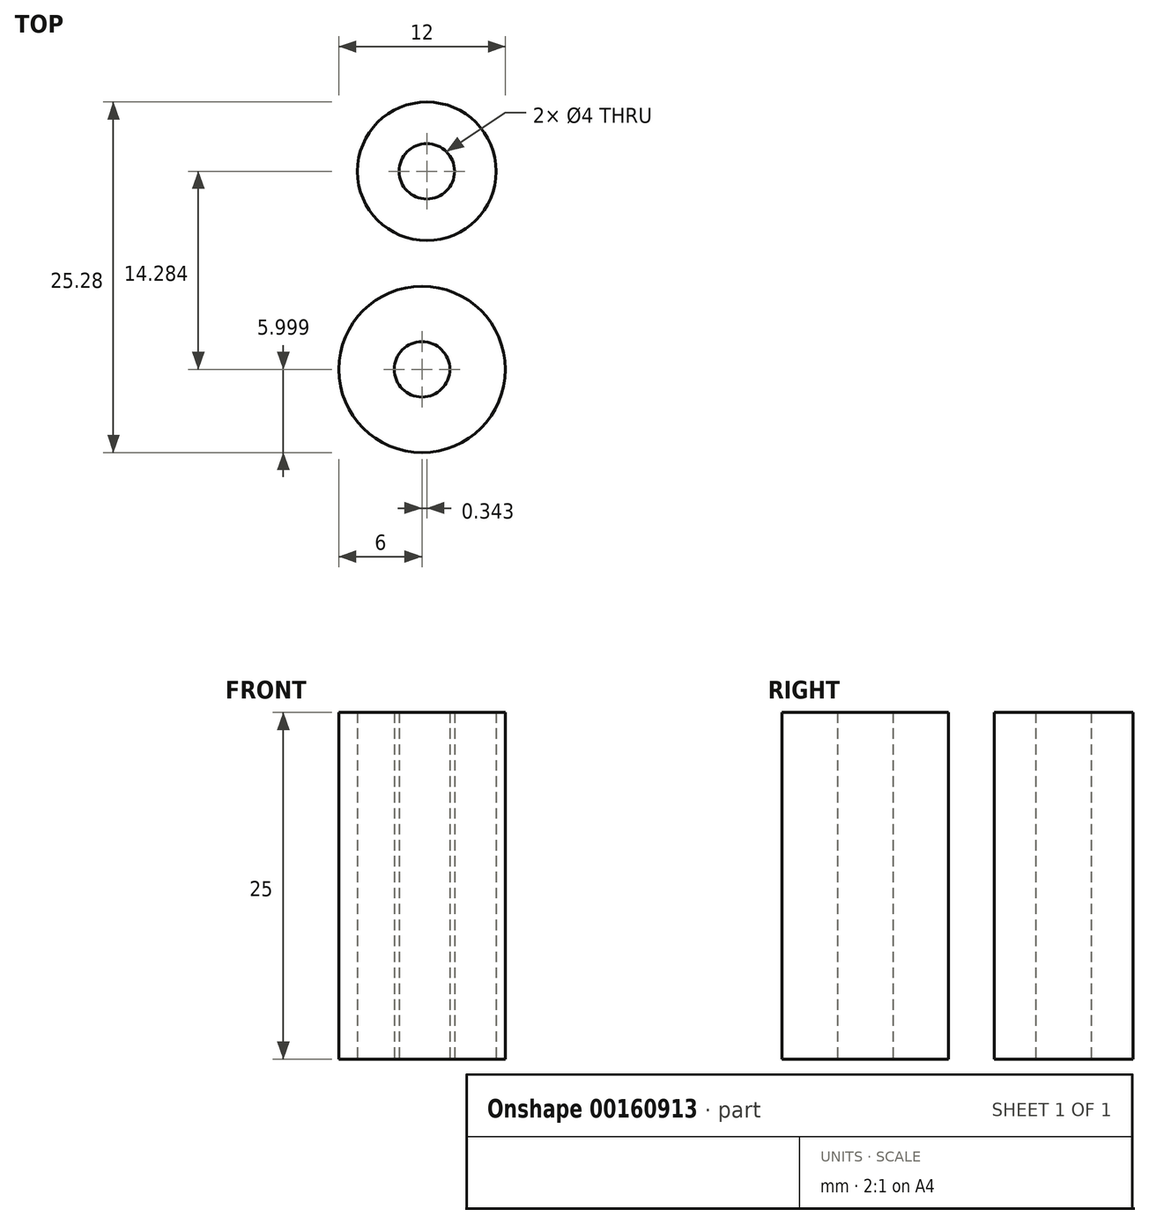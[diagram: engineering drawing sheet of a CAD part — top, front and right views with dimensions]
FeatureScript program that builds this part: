
annotation { "Feature Type Name" : "Feature", "Feature Type Description" : "" }
export const myFeature = defineFeature(function(context is Context, id is Id, definition is map)
    precondition{}
    {
        {
            var Q0;
            Q0=qCreatedBy(makeId("Top.planeOp"),FACE);
            var sketch = newSketch(context, id + "F0", { "sketchPlane" : qUnion([Q0])});
            skCircle(sketch, "E0", {"center": v(-39.6, 18.8) * mm, "radius": 2 * mm});
            skCircle(sketch, "E1", {"center": v(-39.6, 18.8) * mm, "radius": 5 * mm});
            skCircle(sketch, "E2", {"center": v(-39.95, 4.52) * mm, "radius": 2 * mm});
            skCircle(sketch, "E3", {"center": v(-39.95, 4.52) * mm, "radius": 6 * mm});
            skSolve(sketch);
        }
        {
            var Q0;
            Q0 = qSketchRegion(id + "F0", true);
            extrude(context, id + "F1", {"entities" : qUnion([Q0]), "depth" : 25 * mm});
        }
    });
